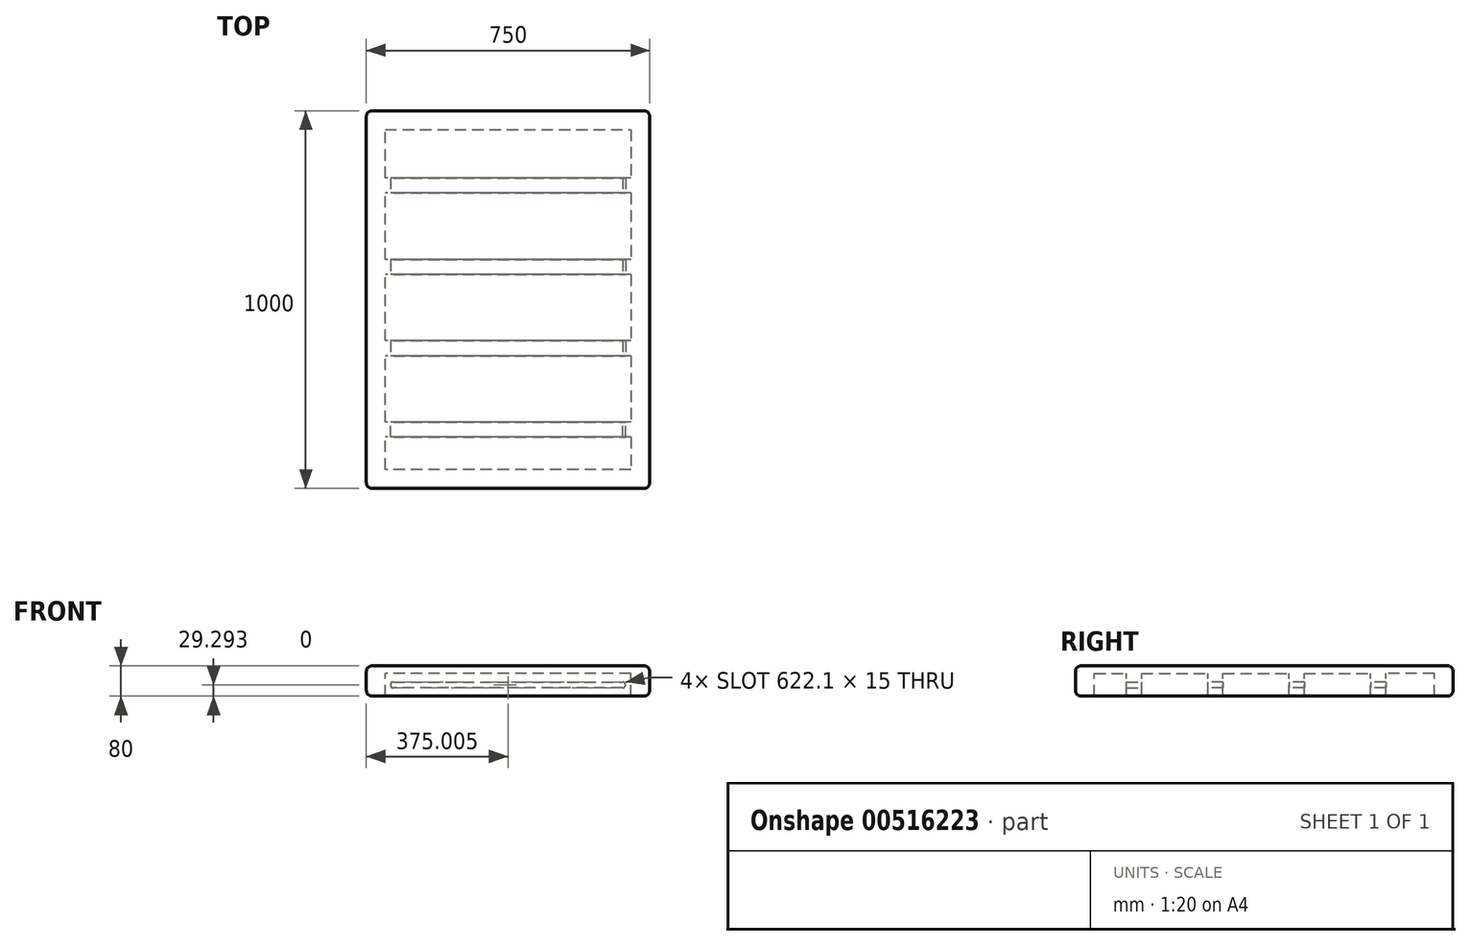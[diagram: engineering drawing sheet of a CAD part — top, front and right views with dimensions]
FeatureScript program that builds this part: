
annotation { "Feature Type Name" : "Feature", "Feature Type Description" : "" }
export const myFeature = defineFeature(function(context is Context, id is Id, definition is map)
    precondition{}
    {
        {
            var Q0;
            Q0=qCreatedBy(makeId("Top.planeOp"),FACE);
            var sketch = newSketch(context, id + "F0", { "sketchPlane" : qUnion([Q0])});
            skLineSegment(sketch, "E0.bottom", {"start": v(0, 0) * mm, "end": v(750, 0) * mm});
            skLineSegment(sketch, "E0.top", {"start": v(0, 1000) * mm, "end": v(750, 1000) * mm});
            skLineSegment(sketch, "E0.left", {"start": v(0, 0) * mm, "end": v(0, 1000) * mm});
            skLineSegment(sketch, "E0.right", {"start": v(750, 0) * mm, "end": v(750, 1000) * mm});
            skSolve(sketch);
        }
        {
            var Q0;
            Q0=makeQuery(id+"F0.imprint","IMPRINT",FACE,{"disambiguationData":[TD([[makeQuery(id+"F0.imprint","IMPRINT",EDGE,{"derivedFrom":sQuery(id+"F0.wireOp",EDGE,"E0.bottom")}),1.0]])]});
            extrude(context, id + "F1", {"entities" : qUnion([Q0]), "depth" : 20 * mm, "offsetDistance" : 25 * mm});
        }
        {
            var Q0;
            Q0=makeQuery(id+"F1.opExtrude","CAP_FACE",FACE,{"disambiguationData":[OSD([sQuery(id+"F0.wireOp",EDGE,"E0.bottom"),sQuery(id+"F0.wireOp",EDGE,"E0.top"),sQuery(id+"F0.wireOp",EDGE,"E0.left"),sQuery(id+"F0.wireOp",EDGE,"E0.right")])],"isStart":true});
            var sketch = newSketch(context, id + "F2", { "sketchPlane" : qUnion([Q0])});
            skLineSegment(sketch, "E1.0", {"start": v(50, -950) * mm, "end": v(700, -950) * mm});
            skLineSegment(sketch, "E1.1", {"start": v(50, -50) * mm, "end": v(50, -950) * mm});
            skLineSegment(sketch, "E1.2", {"start": v(700, -50) * mm, "end": v(50, -50) * mm});
            skLineSegment(sketch, "E1.3", {"start": v(700, -950) * mm, "end": v(700, -50) * mm});
            skLineSegment(sketch, "E2.0", {"start": v(0, -1000) * mm, "end": v(750, -1000) * mm});
            skLineSegment(sketch, "E2.1", {"start": v(0, 0) * mm, "end": v(0, -1000) * mm});
            skLineSegment(sketch, "E2.2", {"start": v(750, 0) * mm, "end": v(0, 0) * mm});
            skLineSegment(sketch, "E2.3", {"start": v(750, -1000) * mm, "end": v(750, 0) * mm});
            skSolve(sketch);
        }
        {
            var Q0;
            Q0 = qSketchRegion(id + "F2", true);
            extrude(context, id + "F3", {"entities" : qUnion([Q0]), "operationType" : NewBodyOperationType.ADD, "depth" : 60 * mm, "offsetDistance" : 25 * mm});
        }
        {
            var Q0;
            Q0=makeQuery(id+"F3.boolean.opBoolean","MERGE",FACE,{"derivedFrom":[makeQuery(id+"F1.opExtrude","SWEPT_FACE",FACE,{"disambiguationData":[OSD([sQuery(id+"F0.wireOp",EDGE,"E0.right")])]}),makeQuery(id+"F3.opExtrude","SWEPT_FACE",FACE,{"disambiguationData":[OSD([sQuery(id+"F2.wireOp",EDGE,"E2.3")])]})]});
            var Q1;
            Q1=makeQuery(id+"F3.boolean.opBoolean","MERGE",FACE,{"derivedFrom":[makeQuery(id+"F1.opExtrude","SWEPT_FACE",FACE,{"disambiguationData":[OSD([sQuery(id+"F0.wireOp",EDGE,"E0.bottom")])]}),makeQuery(id+"F3.opExtrude","SWEPT_FACE",FACE,{"disambiguationData":[OSD([sQuery(id+"F2.wireOp",EDGE,"E2.2")])]})]});
            var Q2;
            Q2=makeQuery(id+"F3.boolean.opBoolean","MERGE",FACE,{"derivedFrom":[makeQuery(id+"F1.opExtrude","SWEPT_FACE",FACE,{"disambiguationData":[OSD([sQuery(id+"F0.wireOp",EDGE,"E0.left")])]}),makeQuery(id+"F3.opExtrude","SWEPT_FACE",FACE,{"disambiguationData":[OSD([sQuery(id+"F2.wireOp",EDGE,"E2.1")])]})]});
            var Q3;
            Q3=makeQuery(id+"F3.boolean.opBoolean","MERGE",FACE,{"derivedFrom":[makeQuery(id+"F1.opExtrude","SWEPT_FACE",FACE,{"disambiguationData":[OSD([sQuery(id+"F0.wireOp",EDGE,"E0.top")])]}),makeQuery(id+"F3.opExtrude","SWEPT_FACE",FACE,{"disambiguationData":[OSD([sQuery(id+"F2.wireOp",EDGE,"E2.0")])]})]});
            fillet(context, id + "F4", {"entities" : qUnion([Q0, Q1, Q2, Q3]), "radius" : 15 * mm, "tangentPropagation" : true, "allowEdgeOverflow" : false});
        }
        {
            var Q0;
            Q0=makeQuery(id+"F1.opExtrude","CAP_FACE",FACE,{"disambiguationData":[OSD([sQuery(id+"F0.wireOp",EDGE,"E0.bottom"),sQuery(id+"F0.wireOp",EDGE,"E0.top"),sQuery(id+"F0.wireOp",EDGE,"E0.left"),sQuery(id+"F0.wireOp",EDGE,"E0.right")])],"isStart":true});
            var sketch = newSketch(context, id + "F5", { "sketchPlane" : qUnion([Q0])});
            skLineSegment(sketch, "E3.bottom", {"start": v(700, -135.55) * mm, "end": v(50, -135.55) * mm});
            skLineSegment(sketch, "E3.top", {"start": v(700, -175.55) * mm, "end": v(50, -175.55) * mm});
            skLineSegment(sketch, "E3.left", {"start": v(700, -135.55) * mm, "end": v(700, -175.55) * mm});
            skLineSegment(sketch, "E3.right", {"start": v(50, -135.55) * mm, "end": v(50, -175.55) * mm});
            skLineSegment(sketch, "E4.bottom", {"start": v(700, -391.09) * mm, "end": v(50, -391.09) * mm});
            skLineSegment(sketch, "E4.top", {"start": v(700, -351.09) * mm, "end": v(50, -351.09) * mm});
            skLineSegment(sketch, "E4.left", {"start": v(700, -391.09) * mm, "end": v(700, -351.09) * mm});
            skLineSegment(sketch, "E4.right", {"start": v(50, -391.09) * mm, "end": v(50, -351.09) * mm});
            skLineSegment(sketch, "E5.bottom", {"start": v(700, -566.02) * mm, "end": v(50, -566.02) * mm});
            skLineSegment(sketch, "E5.top", {"start": v(700, -606.02) * mm, "end": v(50, -606.02) * mm});
            skLineSegment(sketch, "E5.left", {"start": v(700, -566.02) * mm, "end": v(700, -606.02) * mm});
            skLineSegment(sketch, "E5.right", {"start": v(50, -566.02) * mm, "end": v(50, -606.02) * mm});
            skLineSegment(sketch, "E6.bottom", {"start": v(700, -782.12) * mm, "end": v(50, -782.12) * mm});
            skLineSegment(sketch, "E6.top", {"start": v(700, -822.12) * mm, "end": v(50, -822.12) * mm});
            skLineSegment(sketch, "E6.left", {"start": v(700, -782.12) * mm, "end": v(700, -822.12) * mm});
            skLineSegment(sketch, "E6.right", {"start": v(50, -782.12) * mm, "end": v(50, -822.12) * mm});
            skSolve(sketch);
        }
        {
            var Q0;
            Q0 = qSketchRegion(id + "F5", true);
            extrude(context, id + "F6", {"entities" : qUnion([Q0]), "operationType" : NewBodyOperationType.ADD, "depth" : 60 * mm, "offsetDistance" : 25 * mm});
        }
        {
            var Q0;
            Q0=makeQuery(id+"F6.opExtrude","SWEPT_FACE",FACE,{"disambiguationData":[OSD([sQuery(id+"F5.wireOp",EDGE,"E4.top")])]});
            var sketch = newSketch(context, id + "F7", { "sketchPlane" : qUnion([Q0])});
            skArc(sketch, "E7", {"start": v(678.37, -38.2) * mm, "mid": v(686.05, -30.8) * mm, "end": v(678.56, -23.2) * mm});
            skArc(sketch, "E8.MirrorC", {"start": v(71.45, -38.2) * mm, "mid": v(63.95, -30.7) * mm, "end": v(71.45, -23.2) * mm});
            skLineSegment(sketch, "E9", {"start": v(71.45, -23.2) * mm, "end": v(678.56, -23.2) * mm});
            skLineSegment(sketch, "E10", {"start": v(678.74, -38.2) * mm, "end": v(71.45, -38.2) * mm});
            skSolve(sketch);
        }
        {
            var Q0;
            Q0 = qSketchRegion(id + "F7", true);
            extrude(context, id + "F8", {"entities" : qUnion([Q0]), "operationType" : NewBodyOperationType.REMOVE, "oppositeDirection" : true, "depth" : 500 * mm, "offsetDistance" : 25 * mm});
        }
        {
            var Q0;
            Q0=makeQuery(id+"F6.opExtrude","SWEPT_FACE",FACE,{"disambiguationData":[OSD([sQuery(id+"F5.wireOp",EDGE,"E4.top")])]});
            var sketch = newSketch(context, id + "F9", { "sketchPlane" : qUnion([Q0])});
            skLineSegment(sketch, "E11.0", {"start": v(71.45, -23.2) * mm, "end": v(678.56, -23.2) * mm});
            skArc(sketch, "E11.1", {"start": v(71.45, -38.2) * mm, "mid": v(63.95, -30.7) * mm, "end": v(71.45, -23.2) * mm});
            skLineSegment(sketch, "E11.2", {"start": v(678.37, -38.2) * mm, "end": v(71.45, -38.2) * mm});
            skArc(sketch, "E11.3", {"start": v(678.37, -38.2) * mm, "mid": v(686.05, -30.8) * mm, "end": v(678.56, -23.2) * mm});
            skSolve(sketch);
        }
        {
            var Q0;
            Q0 = qSketchRegion(id + "F9", true);
            extrude(context, id + "F10", {"entities" : qUnion([Q0]), "operationType" : NewBodyOperationType.REMOVE, "depth" : 242 * mm, "offsetDistance" : 25 * mm});
        }
    });
